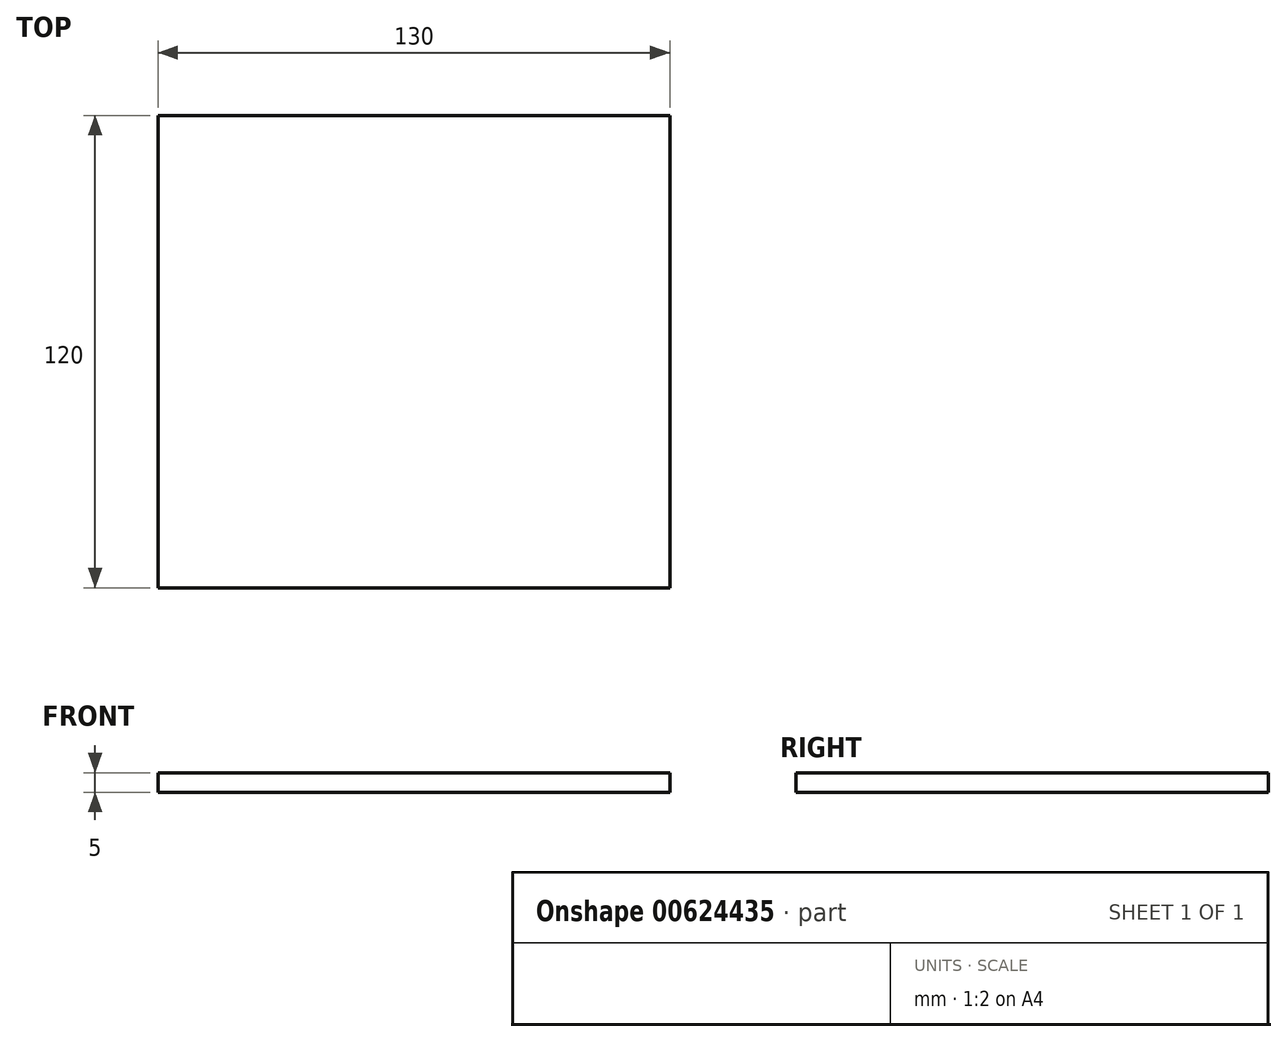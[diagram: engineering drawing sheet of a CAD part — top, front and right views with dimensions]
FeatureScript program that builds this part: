
annotation { "Feature Type Name" : "Feature", "Feature Type Description" : "" }
export const myFeature = defineFeature(function(context is Context, id is Id, definition is map)
    precondition{}
    {
        {
            var Q0;
            Q0=qCreatedBy(makeId("Top.planeOp"),FACE);
            var sketch = newSketch(context, id + "F0", { "sketchPlane" : qUnion([Q0])});
            skLineSegment(sketch, "E0.bottom", {"start": v(65, -60) * mm, "end": v(-65, -60) * mm});
            skLineSegment(sketch, "E0.top", {"start": v(65, 60) * mm, "end": v(-65, 60) * mm});
            skLineSegment(sketch, "E0.left", {"start": v(65, -60) * mm, "end": v(65, 60) * mm});
            skLineSegment(sketch, "E0.right", {"start": v(-65, -60) * mm, "end": v(-65, 60) * mm});
            skPoint(sketch, "E0.middle", {"position": v(0, 0) * mm});
            skSolve(sketch);
        }
        {
            var Q0;
            Q0 = qSketchRegion(id + "F0", true);
            extrude(context, id + "F1", {"entities" : qUnion([Q0]), "depth" : 5 * mm, "offsetDistance" : 25.4 * mm});
        }
    });
